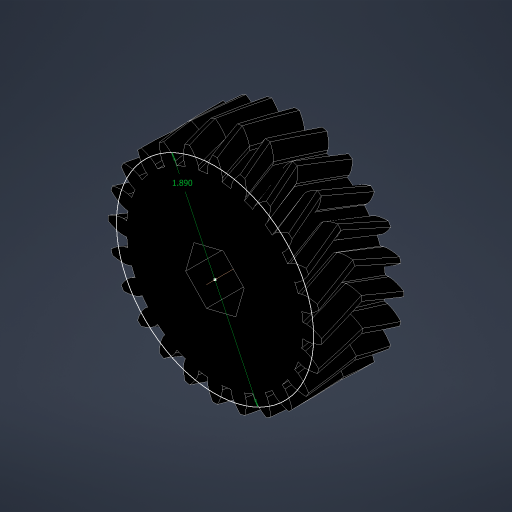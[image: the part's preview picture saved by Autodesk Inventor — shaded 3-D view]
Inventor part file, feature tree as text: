
AUTODESK INVENTOR PART (.ipt)
format: ipt  version: 2023.4 (Build 274418000, 418)  size: 868,864 bytes
history: native  units: in
note: dims shown in document units (in); Inventor stores cm internally (conversion verified against a paired STEP export)
features: sketch x2, extrude x1, other x1
ambient origin geometry x8: Origin, YZ Plane, XZ Plane, XY Plane, X Axis, Y Axis, Z Axis, Center Point
bodies: Solid1 (feature_tree)
feature tree (4):
  extrude  "Extrusion1"  TaperAngle=0.0deg  [1 undecoded]
  sketch  "Sketch3"  dims[d5=1.8898in]
  sketch  "Sketch1"  dims[d0=0.5in d1=0.0in d2=0.0in]
  other  "Helical 2M 24T"
note: 1 required parameter value undecoded (feature->parameter linkage not recoverable at this tier; creation-order binding heuristic only, values carry confidence <= 0.55)
